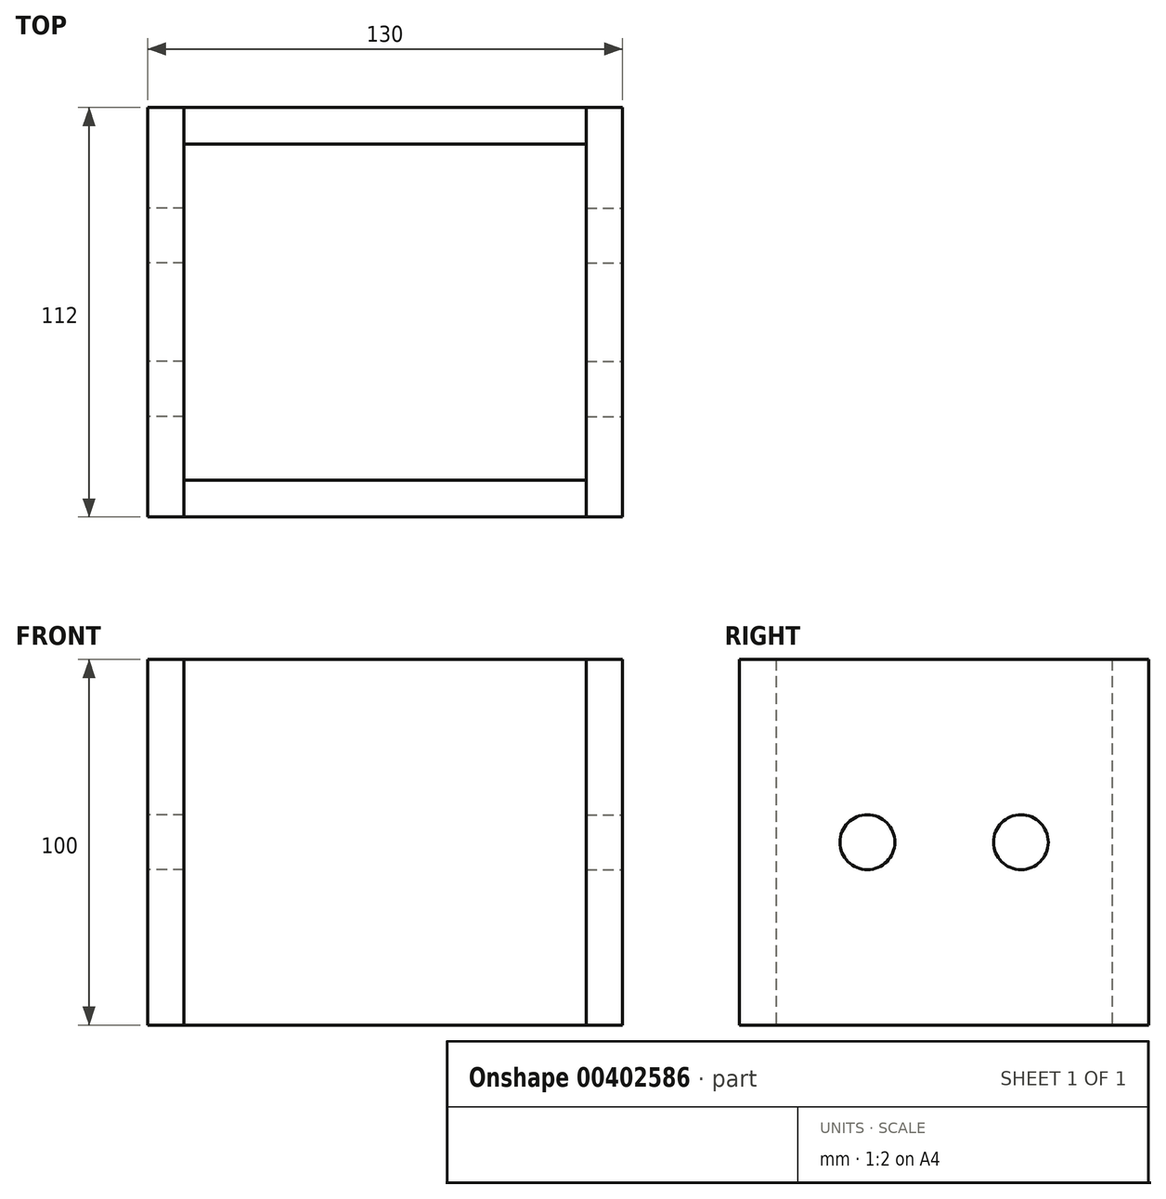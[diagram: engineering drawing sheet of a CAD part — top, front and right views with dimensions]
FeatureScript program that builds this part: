
annotation { "Feature Type Name" : "Feature", "Feature Type Description" : "" }
export const myFeature = defineFeature(function(context is Context, id is Id, definition is map)
    precondition{}
    {
        {
            var Q0;
            Q0=qCreatedBy(makeId("Right.planeOp"),FACE);
            var sketch = newSketch(context, id + "F0", { "sketchPlane" : qUnion([Q0])});
            skLineSegment(sketch, "E0.bottom", {"start": v(-35, 50) * mm, "end": v(21, 50) * mm});
            skLineSegment(sketch, "E0.top", {"start": v(-35, -50) * mm, "end": v(21, -50) * mm});
            skLineSegment(sketch, "E0.left", {"start": v(-35, 50) * mm, "end": v(-35, -50) * mm});
            skLineSegment(sketch, "E0.right", {"start": v(21, 50) * mm, "end": v(21, -50) * mm});
            skCircle(sketch, "E1", {"center": v(0, 0) * mm, "radius": 7.5 * mm});
            skSolve(sketch);
        }
        {
            var Q0;
            Q0=makeQuery(id+"F0.imprint","IMPRINT",FACE,{"disambiguationData":[TD([[makeQuery(id+"F0.imprint","IMPRINT",EDGE,{"derivedFrom":sQuery(id+"F0.wireOp",EDGE,"E0.bottom")}),-1.0]])]});
            extrude(context, id + "F1", {"entities" : qUnion([Q0]), "depth" : 10 * mm});
        }
        {
            var Q0;
            Q0=makeQuery(id+"F1.opExtrude","SWEPT_BODY",BODY,{"disambiguationData":[OSD([sQuery(id+"F0.wireOp",EDGE,"E0.bottom"),sQuery(id+"F0.wireOp",EDGE,"E0.top"),sQuery(id+"F0.wireOp",EDGE,"E0.left"),sQuery(id+"F0.wireOp",EDGE,"E0.right"),sQuery(id+"F0.wireOp",EDGE,"rgaBh7ed-yzeX-51PE-KJwg-0XFkLaL4d9ET"),sQuery(id+"F0.wireOp",EDGE,"PRCWQJZA-zwb4-kcCU-vDn6-fWhEnT45CPGa"),sQuery(id+"F0.wireOp",EDGE,"24f5492e-8ac3-413e-9412-904b776a6be8.trimOffspring"),sQuery(id+"F0.wireOp",EDGE,"954fe64b-5e16-4ffe-b02d-878927013ef90.MirrorCS")])]});
            var Q1;
            Q1=makeQuery(id+"F1.opExtrude","SWEPT_FACE",FACE,{"disambiguationData":[OSD([sQuery(id+"F0.wireOp",EDGE,"E0.right")])]});
            mirror(context, id + "F2", {"operationType" : NewBodyOperationType.ADD, "entities" : qUnion([Q0]), "mirrorPlane" : qUnion([Q1])});
        }
        {
            var Q0;
            {var subQ0=makeQuery(id+"F1.opExtrude","CAP_FACE",FACE,{"disambiguationData":[OSD([sQuery(id+"F0.wireOp",EDGE,"E0.bottom"),sQuery(id+"F0.wireOp",EDGE,"E0.top"),sQuery(id+"F0.wireOp",EDGE,"E0.left"),sQuery(id+"F0.wireOp",EDGE,"E0.right"),sQuery(id+"F0.wireOp",EDGE,"rgaBh7ed-yzeX-51PE-KJwg-0XFkLaL4d9ET"),sQuery(id+"F0.wireOp",EDGE,"PRCWQJZA-zwb4-kcCU-vDn6-fWhEnT45CPGa"),sQuery(id+"F0.wireOp",EDGE,"24f5492e-8ac3-413e-9412-904b776a6be8.trimOffspring"),sQuery(id+"F0.wireOp",EDGE,"954fe64b-5e16-4ffe-b02d-878927013ef90.MirrorCS")])],"isStart":false});Q0=makeQuery(id+"F2.boolean.opBoolean","MERGE",FACE,{"derivedFrom":[subQ0,makeQuery(id+"F2.opPattern","COPY",FACE,{"derivedFrom":subQ0,"instanceName":"1"})]});}
            var sketch = newSketch(context, id + "F3", { "sketchPlane" : qUnion([Q0])});
            skLineSegment(sketch, "E2.0", {"start": v(-35, 50) * mm, "end": v(-35, -50) * mm});
            skLineSegment(sketch, "E3.0", {"start": v(-35, 50) * mm, "end": v(21, 50) * mm});
            skLineSegment(sketch, "E4.0", {"start": v(-35, -50) * mm, "end": v(21, -50) * mm});
            skLineSegment(sketch, "E5", {"start": v(-25, 50) * mm, "end": v(-25, -50) * mm});
            skSolve(sketch);
        }
        {
            var Q0;
            Q0 = qSketchRegion(id + "F3", true);
            extrude(context, id + "F4", {"entities" : qUnion([Q0]), "depth" : 110 * mm});
        }
        {
            var Q0;
            Q0=makeQuery(id+"F2.opPattern","COPY",FACE,{"derivedFrom":makeQuery(id+"F1.opExtrude","SWEPT_FACE",FACE,{"disambiguationData":[OSD([sQuery(id+"F0.wireOp",EDGE,"E0.left")])]}),"instanceName":"1"});
            var Q1;
            Q1=makeQuery(id+"F1.opExtrude","SWEPT_FACE",FACE,{"disambiguationData":[OSD([sQuery(id+"F0.wireOp",EDGE,"E0.left")])]});
            cPlane(context, id + "F5", {"entities" : qUnion([Q0, Q1]), "cplaneType" : CPlaneType.MID_PLANE, "offset" : 25 * mm, "width" : 150 * mm, "height" : 150 * mm});
        }
        {
            var Q0;
            Q0=makeQuery(id+"F4.opExtrude","SWEPT_BODY",BODY,{"disambiguationData":[OSD([sQuery(id+"F3.wireOp",EDGE,"E2.0"),sQuery(id+"F3.wireOp",EDGE,"E3.0"),sQuery(id+"F3.wireOp",EDGE,"E4.0"),sQuery(id+"F3.wireOp",EDGE,"E5")])]});
            var Q1;
            Q1=qCreatedBy(id+"F5.planeOp",FACE);
            mirror(context, id + "F6", {"entities" : qUnion([Q0]), "mirrorPlane" : qUnion([Q1])});
        }
        {
            var Q0;
            {var subQ0=makeQuery(id+"F1.opExtrude","CAP_FACE",FACE,{"disambiguationData":[OSD([sQuery(id+"F0.wireOp",EDGE,"E0.bottom"),sQuery(id+"F0.wireOp",EDGE,"E0.top"),sQuery(id+"F0.wireOp",EDGE,"E0.left"),sQuery(id+"F0.wireOp",EDGE,"E0.right"),sQuery(id+"F0.wireOp",EDGE,"rgaBh7ed-yzeX-51PE-KJwg-0XFkLaL4d9ET"),sQuery(id+"F0.wireOp",EDGE,"PRCWQJZA-zwb4-kcCU-vDn6-fWhEnT45CPGa"),sQuery(id+"F0.wireOp",EDGE,"24f5492e-8ac3-413e-9412-904b776a6be8.trimOffspring"),sQuery(id+"F0.wireOp",EDGE,"954fe64b-5e16-4ffe-b02d-878927013ef90.MirrorCS")])],"isStart":false});Q0=makeQuery(id+"F2.boolean.opBoolean","MERGE",FACE,{"derivedFrom":[subQ0,makeQuery(id+"F2.opPattern","COPY",FACE,{"derivedFrom":subQ0,"instanceName":"1"})]});}
            var Q1;
            Q1=makeQuery(id+"F4.opExtrude","CAP_FACE",FACE,{"disambiguationData":[OSD([sQuery(id+"F3.wireOp",EDGE,"E2.0"),sQuery(id+"F3.wireOp",EDGE,"E3.0"),sQuery(id+"F3.wireOp",EDGE,"E4.0"),sQuery(id+"F3.wireOp",EDGE,"E5")])],"isStart":false});
            cPlane(context, id + "F7", {"entities" : qUnion([Q0, Q1]), "cplaneType" : CPlaneType.MID_PLANE, "offset" : 25 * mm, "width" : 150 * mm, "height" : 150 * mm});
        }
        {
            var Q0;
            Q0=makeQuery(id+"F1.opExtrude","SWEPT_BODY",BODY,{"disambiguationData":[OSD([sQuery(id+"F0.wireOp",EDGE,"E0.bottom"),sQuery(id+"F0.wireOp",EDGE,"E0.top"),sQuery(id+"F0.wireOp",EDGE,"E0.left"),sQuery(id+"F0.wireOp",EDGE,"E0.right"),sQuery(id+"F0.wireOp",EDGE,"rgaBh7ed-yzeX-51PE-KJwg-0XFkLaL4d9ET"),sQuery(id+"F0.wireOp",EDGE,"PRCWQJZA-zwb4-kcCU-vDn6-fWhEnT45CPGa"),sQuery(id+"F0.wireOp",EDGE,"24f5492e-8ac3-413e-9412-904b776a6be8.trimOffspring"),sQuery(id+"F0.wireOp",EDGE,"954fe64b-5e16-4ffe-b02d-878927013ef90.MirrorCS")])]});
            var Q1;
            Q1=qCreatedBy(id+"F7.planeOp",FACE);
            mirror(context, id + "F8", {"entities" : qUnion([Q0]), "mirrorPlane" : qUnion([Q1])});
        }
    });
